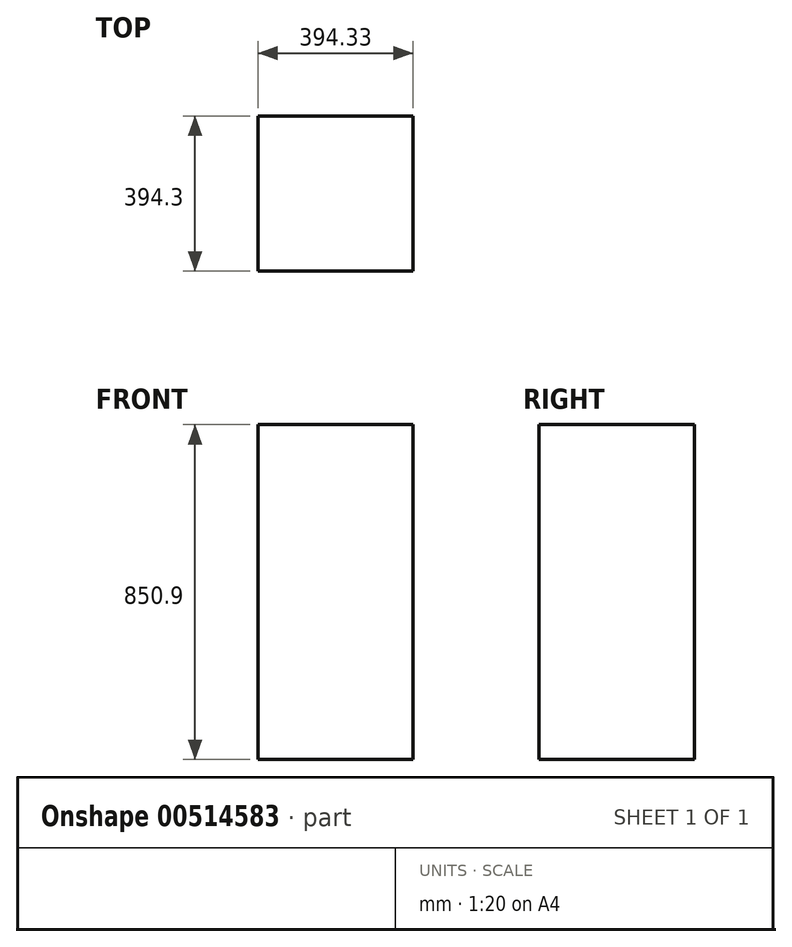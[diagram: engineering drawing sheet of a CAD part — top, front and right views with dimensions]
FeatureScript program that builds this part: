
annotation { "Feature Type Name" : "Feature", "Feature Type Description" : "" }
export const myFeature = defineFeature(function(context is Context, id is Id, definition is map)
    precondition{}
    {
        {
            var Q0;
            Q0=qCreatedBy(makeId("Top.planeOp"),FACE);
            var sketch = newSketch(context, id + "F0", { "sketchPlane" : qUnion([Q0])});
            skLineSegment(sketch, "E0.bottom", {"start": v(-107.36, 119.64) * mm, "end": v(286.97, 119.64) * mm});
            skLineSegment(sketch, "E0.top", {"start": v(-107.36, -274.66) * mm, "end": v(286.97, -274.66) * mm});
            skLineSegment(sketch, "E0.left", {"start": v(-107.36, 119.64) * mm, "end": v(-107.36, -274.66) * mm});
            skLineSegment(sketch, "E0.right", {"start": v(286.97, 119.64) * mm, "end": v(286.97, -274.66) * mm});
            skSolve(sketch);
        }
        {
            var Q0;
            Q0=makeQuery(id+"F0.imprint","IMPRINT",FACE,{"disambiguationData":[TD([[makeQuery(id+"F0.imprint","IMPRINT",EDGE,{"derivedFrom":sQuery(id+"F0.wireOp",EDGE,"E0.bottom")}),-1.0]])]});
            extrude(context, id + "F1", {"entities" : qUnion([Q0]), "depth" : 850.9 * mm, "offsetDistance" : 25.4 * mm});
        }
    });
